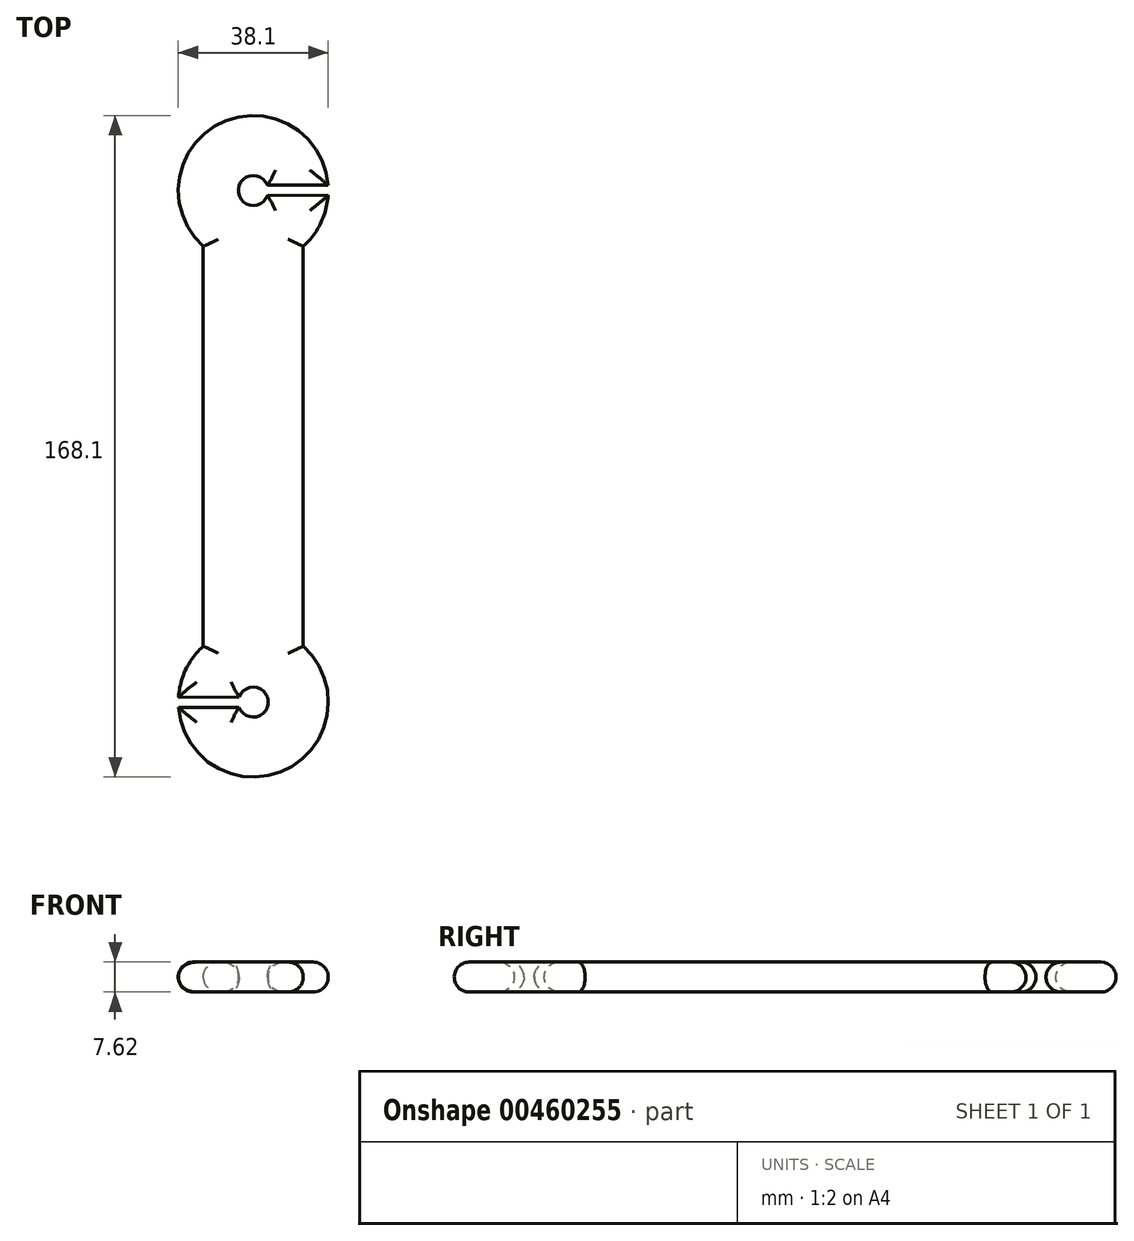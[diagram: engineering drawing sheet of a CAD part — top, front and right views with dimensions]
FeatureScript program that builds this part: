
annotation { "Feature Type Name" : "Feature", "Feature Type Description" : "" }
export const myFeature = defineFeature(function(context is Context, id is Id, definition is map)
    precondition{}
    {
        {
            var Q0;
            Q0=qCreatedBy(makeId("Top.planeOp"),FACE);
            var sketch = newSketch(context, id + "F0", { "sketchPlane" : qUnion([Q0])});
            skArc(sketch, "E0", {"start": v(12.7, 50.8) * mm, "mid": v(17.13, 56.66) * mm, "end": v(19.01, 63.77) * mm});
            skArc(sketch, "E1.MirrorC", {"start": v(12.7, -50.8) * mm, "mid": v(8.37, -82.11) * mm, "end": v(-19, -66.3) * mm});
            skLineSegment(sketch, "E2", {"start": v(-12.7, -50.8) * mm, "end": v(-12.7, 50.8) * mm});
            skLineSegment(sketch, "E3.MirrorCS", {"start": v(12.7, -50.8) * mm, "end": v(12.7, 50.8) * mm});
            skArc(sketch, "E4", {"start": v(3.58, 66.3) * mm, "mid": v(-3.81, 65) * mm, "end": v(3.58, 63.69) * mm});
            skArc(sketch, "E5.MirrorC", {"start": v(-3.58, -63.69) * mm, "mid": v(3.8, -65) * mm, "end": v(-3.58, -66.3) * mm});
            skLineSegment(sketch, "E6", {"start": v(3.58, 66.3) * mm, "end": v(19, 66.3) * mm});
            skLineSegment(sketch, "E7.MirrorCS", {"start": v(3.58, 63.69) * mm, "end": v(19.01, 63.77) * mm});
            skArc(sketch, "E8.trimOffspring", {"start": v(19, 66.3) * mm, "mid": v(-8.37, 82.11) * mm, "end": v(-12.7, 50.8) * mm});
            skLineSegment(sketch, "E9.MirrorCS", {"start": v(-3.58, -63.69) * mm, "end": v(-19.01, -63.77) * mm});
            skLineSegment(sketch, "E10.MirrorCS", {"start": v(-3.58, -66.3) * mm, "end": v(-19, -66.3) * mm});
            skArc(sketch, "E11.trimOffspring", {"start": v(-19.01, -63.77) * mm, "mid": v(-17.13, -56.66) * mm, "end": v(-12.7, -50.8) * mm});
            skSolve(sketch);
        }
        {
            var Q0;
            Q0 = qSketchRegion(id + "F0", true);
            extrude(context, id + "F1", {"entities" : qUnion([Q0]), "depth" : 7.62 * mm});
        }
        {
            var Q0;
            Q0=makeQuery(id+"F1.opExtrude","CAP_FACE",FACE,{"disambiguationData":[OSD([sQuery(id+"F0.wireOp",EDGE,"E0"),sQuery(id+"F0.wireOp",EDGE,"E1.MirrorC"),sQuery(id+"F0.wireOp",EDGE,"E2"),sQuery(id+"F0.wireOp",EDGE,"E3.MirrorCS"),sQuery(id+"F0.wireOp",EDGE,"E4"),sQuery(id+"F0.wireOp",EDGE,"E5.MirrorC"),sQuery(id+"F0.wireOp",EDGE,"E6"),sQuery(id+"F0.wireOp",EDGE,"E7.MirrorCS"),sQuery(id+"F0.wireOp",EDGE,"E8.trimOffspring"),sQuery(id+"F0.wireOp",EDGE,"E9.MirrorCS"),sQuery(id+"F0.wireOp",EDGE,"E10.MirrorCS"),sQuery(id+"F0.wireOp",EDGE,"E11.trimOffspring")])],"isStart":true});
            fillet(context, id + "F2", {"entities" : qUnion([Q0]), "radius" : 3.8 * mm, "tangentPropagation" : true, "allowEdgeOverflow" : false});
        }
        {
            var Q0;
            Q0=makeQuery(id+"F1.opExtrude","CAP_FACE",FACE,{"disambiguationData":[OSD([sQuery(id+"F0.wireOp",EDGE,"E0"),sQuery(id+"F0.wireOp",EDGE,"E1.MirrorC"),sQuery(id+"F0.wireOp",EDGE,"E2"),sQuery(id+"F0.wireOp",EDGE,"E3.MirrorCS"),sQuery(id+"F0.wireOp",EDGE,"E4"),sQuery(id+"F0.wireOp",EDGE,"E5.MirrorC"),sQuery(id+"F0.wireOp",EDGE,"E6"),sQuery(id+"F0.wireOp",EDGE,"E7.MirrorCS"),sQuery(id+"F0.wireOp",EDGE,"E8.trimOffspring"),sQuery(id+"F0.wireOp",EDGE,"E9.MirrorCS"),sQuery(id+"F0.wireOp",EDGE,"E10.MirrorCS"),sQuery(id+"F0.wireOp",EDGE,"E11.trimOffspring")])],"isStart":false});
            fillet(context, id + "F3", {"entities" : qUnion([Q0]), "radius" : 3.8 * mm, "tangentPropagation" : true, "allowEdgeOverflow" : false});
        }
    });
